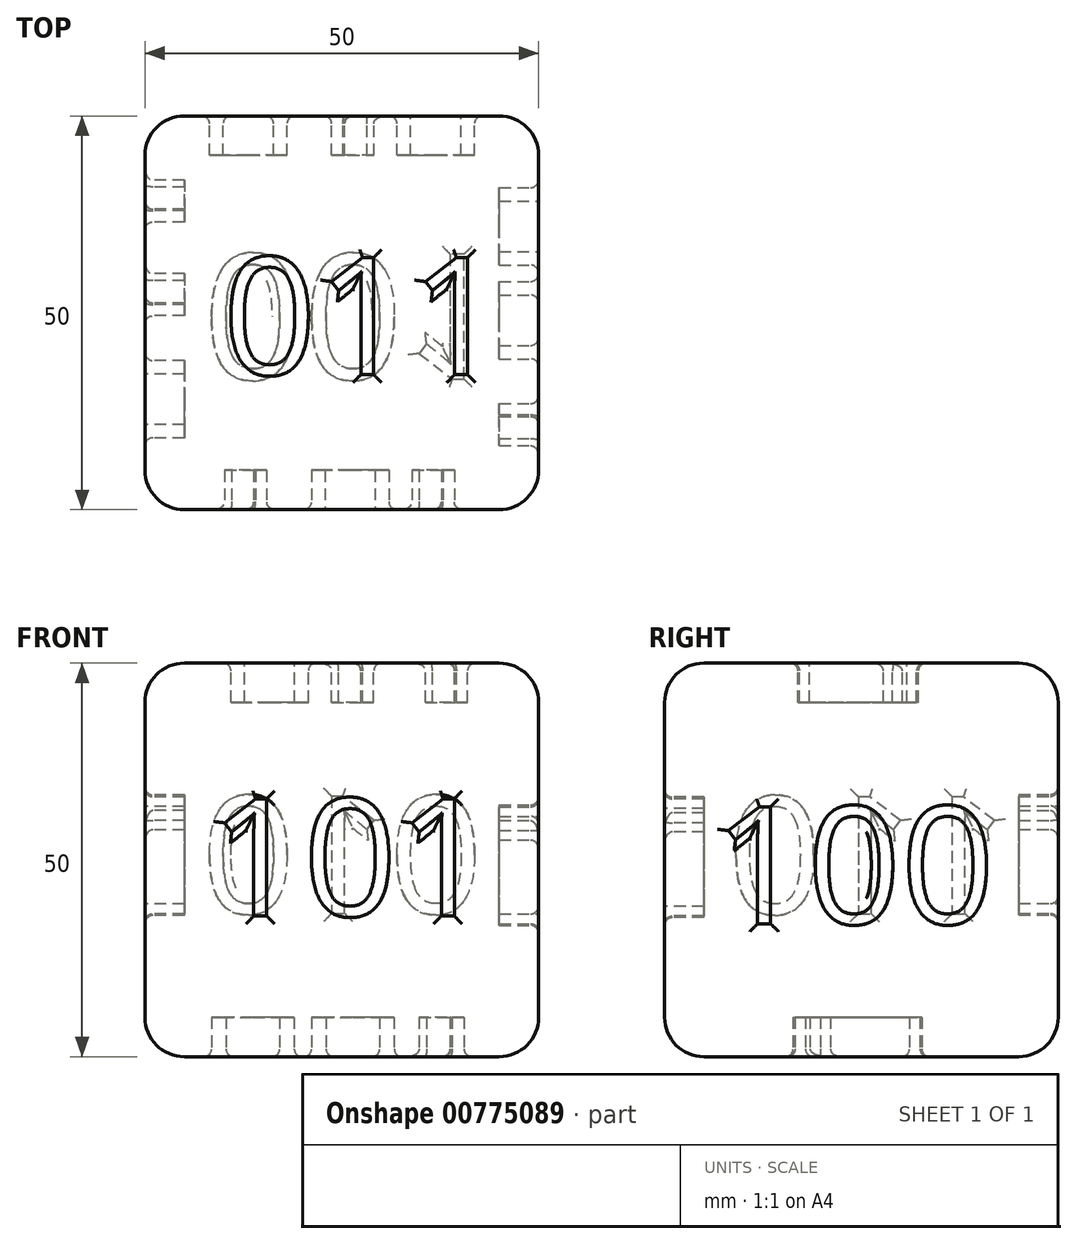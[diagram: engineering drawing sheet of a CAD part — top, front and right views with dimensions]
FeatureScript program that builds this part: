
annotation { "Feature Type Name" : "Feature", "Feature Type Description" : "" }
export const myFeature = defineFeature(function(context is Context, id is Id, definition is map)
    precondition{}
    {
        {
            var Q0;
            Q0=qCreatedBy(makeId("Top.planeOp"),FACE);
            var sketch = newSketch(context, id + "F0", { "sketchPlane" : qUnion([Q0])});
            skPoint(sketch, "E0.middle", {"position": v(0, 0) * mm});
            skLineSegment(sketch, "E1.bottom", {"start": v(25, -25) * mm, "end": v(-25, -25) * mm});
            skLineSegment(sketch, "E1.top", {"start": v(25, 25) * mm, "end": v(-25, 25) * mm});
            skLineSegment(sketch, "E1.left", {"start": v(25, -25) * mm, "end": v(25, 25) * mm});
            skLineSegment(sketch, "E1.right", {"start": v(-25, -25) * mm, "end": v(-25, 25) * mm});
            skSolve(sketch);
        }
        {
            var Q0;
            Q0 = qSketchRegion(id + "F0", true);
            extrude(context, id + "F1", {"entities" : qUnion([Q0]), "depth" : 50 * mm, "offsetDistance" : 25 * mm});
        }
        {
            var Q0;
            Q0=makeQuery(id+"F1.opExtrude","CAP_FACE",FACE,{"disambiguationData":[OSD([sQuery(id+"F0.wireOp",EDGE,"E1.bottom"),sQuery(id+"F0.wireOp",EDGE,"E1.top"),sQuery(id+"F0.wireOp",EDGE,"E1.left"),sQuery(id+"F0.wireOp",EDGE,"E1.right")])],"isStart":true});
            var Q1;
            Q1=makeQuery(id+"F1.opExtrude","SWEPT_FACE",FACE,{"disambiguationData":[OSD([sQuery(id+"F0.wireOp",EDGE,"E1.left")])]});
            var Q2;
            Q2=makeQuery(id+"F1.opExtrude","SWEPT_EDGE",EDGE,{"disambiguationData":[OSD([sQuery(id+"F0.wireOp",EDGE,"E1.bottom"),sQuery(id+"F0.wireOp",EDGE,"E1.right")])]});
            var Q3;
            Q3=makeQuery(id+"F1.opExtrude","CAP_FACE",FACE,{"disambiguationData":[OSD([sQuery(id+"F0.wireOp",EDGE,"E1.bottom"),sQuery(id+"F0.wireOp",EDGE,"E1.top"),sQuery(id+"F0.wireOp",EDGE,"E1.left"),sQuery(id+"F0.wireOp",EDGE,"E1.right")])],"isStart":false});
            var Q4;
            Q4=makeQuery(id+"F1.opExtrude","SWEPT_FACE",FACE,{"disambiguationData":[OSD([sQuery(id+"F0.wireOp",EDGE,"E1.right")])]});
            fillet(context, id + "F2", {"entities" : qUnion([Q0, Q1, Q2, Q3, Q4]), "radius" : 5 * mm, "tangentPropagation" : true, "allowEdgeOverflow" : false});
        }
        {
            var Q0;
            Q0=makeQuery(id+"F1.opExtrude","CAP_FACE",FACE,{"disambiguationData":[OSD([sQuery(id+"F0.wireOp",EDGE,"E1.bottom"),sQuery(id+"F0.wireOp",EDGE,"E1.top"),sQuery(id+"F0.wireOp",EDGE,"E1.left"),sQuery(id+"F0.wireOp",EDGE,"E1.right")])],"isStart":true});
            var sketch = newSketch(context, id + "F3", { "sketchPlane" : qUnion([Q0])});
            skText(sketch, "E2", { "text": "001\n", "fontName": "OpenSans-Regular.ttf"});
            const initialGuessF3  = {"E2": [-0.01764, -0.00745, 1, 0, 0.016]};
            skSetInitialGuess(sketch, initialGuessF3);
            skSolve(sketch);
        }
        {
            var Q0;
            Q0 = qSketchRegion(id + "F3", true);
            extrude(context, id + "F4", {"entities" : qUnion([Q0]), "operationType" : NewBodyOperationType.REMOVE, "oppositeDirection" : true, "depth" : 5 * mm, "offsetDistance" : 25 * mm});
        }
        {
            var Q0;
            Q0=makeQuery(id+"F4.boolean.opBoolean","COPY",EDGE,{"derivedFrom":makeQuery(id+"F4.opExtrude","CAP_EDGE",EDGE,{"disambiguationData":[OSD([sQuery(id+"F3.wireOp",EDGE,"E2.sketch_text.stroke-4")])],"isStart":true})});
            var Q1;
            Q1=makeQuery(id+"F4.boolean.opBoolean","COPY",EDGE,{"derivedFrom":makeQuery(id+"F4.opExtrude","CAP_EDGE",EDGE,{"disambiguationData":[OSD([sQuery(id+"F3.wireOp",EDGE,"E2.sketch_text.stroke-3")])],"isStart":true})});
            var Q2;
            Q2=makeQuery(id+"F4.boolean.opBoolean","COPY",EDGE,{"derivedFrom":makeQuery(id+"F4.opExtrude","CAP_EDGE",EDGE,{"disambiguationData":[OSD([sQuery(id+"F3.wireOp",EDGE,"E2.sketch_text.stroke-2")])],"isStart":true})});
            var Q3;
            Q3=makeQuery(id+"F4.boolean.opBoolean","COPY",EDGE,{"derivedFrom":makeQuery(id+"F4.opExtrude","CAP_EDGE",EDGE,{"disambiguationData":[OSD([sQuery(id+"F3.wireOp",EDGE,"E2.sketch_text.stroke-1")])],"isStart":true})});
            var Q4;
            {var subQ0=sQuery(id+"F0.wireOp",EDGE,"E1.right");var subQ1=sQuery(id+"F0.wireOp",EDGE,"E1.top");var subQ2=sQuery(id+"F0.wireOp",EDGE,"E1.bottom");var subQ3=sQuery(id+"F0.wireOp",EDGE,"E1.left");Q4=makeQuery(id+"F4.boolean.opBoolean","SPLIT",FACE,{"disambiguationData":[TD([makeQuery(id+"F4.opExtrude","SWEPT_FACE",FACE,{"disambiguationData":[OSD([sQuery(id+"F3.wireOp",EDGE,"E2.sketch_text.stroke-0")])]})])],"derivedFrom":makeQuery(id+"F1.opExtrude","CAP_FACE",FACE,{"disambiguationData":[OSD([subQ2,subQ1,subQ3,subQ0])],"isStart":true})});}
            var Q5;
            Q5=makeQuery(id+"F4.boolean.opBoolean","COPY",EDGE,{"derivedFrom":makeQuery(id+"F4.opExtrude","CAP_EDGE",EDGE,{"disambiguationData":[OSD([sQuery(id+"F3.wireOp",EDGE,"E2.sketch_text.stroke-11")])],"isStart":true})});
            var Q6;
            Q6=makeQuery(id+"F4.boolean.opBoolean","SPLIT",FACE,{"disambiguationData":[TD([makeQuery(id+"F4.opExtrude","SWEPT_FACE",FACE,{"disambiguationData":[OSD([sQuery(id+"F3.wireOp",EDGE,"E2.sketch_text.stroke-8")])]})])],"derivedFrom":makeQuery(id+"F1.opExtrude","CAP_FACE",FACE,{"disambiguationData":[OSD([sQuery(id+"F0.wireOp",EDGE,"E1.bottom"),sQuery(id+"F0.wireOp",EDGE,"E1.top"),sQuery(id+"F0.wireOp",EDGE,"E1.left"),sQuery(id+"F0.wireOp",EDGE,"E1.right")])],"isStart":true})});
            var Q7;
            Q7=makeQuery(id+"F4.boolean.opBoolean","SPLIT",FACE,{"disambiguationData":[TD([makeQuery(id+"F4.opExtrude","SWEPT_FACE",FACE,{"disambiguationData":[OSD([sQuery(id+"F3.wireOp",EDGE,"E2.sketch_text.stroke-24")])]})])],"derivedFrom":makeQuery(id+"F1.opExtrude","CAP_FACE",FACE,{"disambiguationData":[OSD([sQuery(id+"F0.wireOp",EDGE,"E1.bottom"),sQuery(id+"F0.wireOp",EDGE,"E1.top"),sQuery(id+"F0.wireOp",EDGE,"E1.left"),sQuery(id+"F0.wireOp",EDGE,"E1.right")])],"isStart":true})});
            var Q8;
            Q8=makeQuery(id+"F4.boolean.opBoolean","COPY",EDGE,{"derivedFrom":makeQuery(id+"F4.opExtrude","CAP_EDGE",EDGE,{"disambiguationData":[OSD([sQuery(id+"F3.wireOp",EDGE,"E2.sketch_text.stroke-33")])],"isStart":true})});
            fillet(context, id + "F5", {"entities" : qUnion([Q0, Q1, Q2, Q3, Q4, Q5, Q6, Q7, Q8]), "radius" : 1 * mm, "tangentPropagation" : true, "allowEdgeOverflow" : false});
        }
        {
            var Q0;
            Q0=makeQuery(id+"F1.opExtrude","SWEPT_FACE",FACE,{"disambiguationData":[OSD([sQuery(id+"F0.wireOp",EDGE,"E1.top")])]});
            var sketch = newSketch(context, id + "F6", { "sketchPlane" : qUnion([Q0])});
            skText(sketch, "E3", { "text": "010", "fontName": "OpenSans-Regular.ttf"});
            const initialGuessF6  = {"E3": [-0.0179, 0.0182, 1, 0, 0.015]};
            skSetInitialGuess(sketch, initialGuessF6);
            skSolve(sketch);
        }
        {
            var Q0;
            Q0 = qSketchRegion(id + "F6", true);
            extrude(context, id + "F7", {"entities" : qUnion([Q0]), "operationType" : NewBodyOperationType.REMOVE, "oppositeDirection" : true, "depth" : 5 * mm, "offsetDistance" : 25 * mm});
        }
        {
            var Q0;
            Q0=makeQuery(id+"F7.boolean.opBoolean","COPY",EDGE,{"derivedFrom":makeQuery(id+"F7.opExtrude","CAP_EDGE",EDGE,{"disambiguationData":[OSD([sQuery(id+"F6.wireOp",EDGE,"E3.sketch_text.stroke-2")])],"isStart":true})});
            var Q1;
            Q1=makeQuery(id+"F7.boolean.opBoolean","COPY",EDGE,{"derivedFrom":makeQuery(id+"F7.opExtrude","CAP_EDGE",EDGE,{"disambiguationData":[OSD([sQuery(id+"F6.wireOp",EDGE,"E3.sketch_text.stroke-3")])],"isStart":true})});
            var Q2;
            Q2=makeQuery(id+"F7.boolean.opBoolean","COPY",EDGE,{"derivedFrom":makeQuery(id+"F7.opExtrude","CAP_EDGE",EDGE,{"disambiguationData":[OSD([sQuery(id+"F6.wireOp",EDGE,"E3.sketch_text.stroke-4")])],"isStart":true})});
            var Q3;
            Q3=makeQuery(id+"F7.boolean.opBoolean","COPY",EDGE,{"derivedFrom":makeQuery(id+"F7.opExtrude","CAP_EDGE",EDGE,{"disambiguationData":[OSD([sQuery(id+"F6.wireOp",EDGE,"E3.sketch_text.stroke-5")])],"isStart":true})});
            var Q4;
            Q4=makeQuery(id+"F7.boolean.opBoolean","COPY",EDGE,{"derivedFrom":makeQuery(id+"F7.opExtrude","CAP_EDGE",EDGE,{"disambiguationData":[OSD([sQuery(id+"F6.wireOp",EDGE,"E3.sketch_text.stroke-6")])],"isStart":true})});
            var Q5;
            Q5=makeQuery(id+"F7.boolean.opBoolean","COPY",EDGE,{"derivedFrom":makeQuery(id+"F7.opExtrude","CAP_EDGE",EDGE,{"disambiguationData":[OSD([sQuery(id+"F6.wireOp",EDGE,"E3.sketch_text.stroke-7")])],"isStart":true})});
            var Q6;
            Q6=makeQuery(id+"F7.boolean.opBoolean","COPY",EDGE,{"derivedFrom":makeQuery(id+"F7.opExtrude","CAP_EDGE",EDGE,{"disambiguationData":[OSD([sQuery(id+"F6.wireOp",EDGE,"E3.sketch_text.stroke-0")])],"isStart":true})});
            var Q7;
            Q7=makeQuery(id+"F7.boolean.opBoolean","COPY",EDGE,{"derivedFrom":makeQuery(id+"F7.opExtrude","CAP_EDGE",EDGE,{"disambiguationData":[OSD([sQuery(id+"F6.wireOp",EDGE,"E3.sketch_text.stroke-1")])],"isStart":true})});
            var Q8;
            Q8=makeQuery(id+"F7.boolean.opBoolean","COPY",EDGE,{"derivedFrom":makeQuery(id+"F7.opExtrude","CAP_EDGE",EDGE,{"disambiguationData":[OSD([sQuery(id+"F6.wireOp",EDGE,"E3.sketch_text.stroke-11")])],"isStart":true})});
            var Q9;
            Q9=makeQuery(id+"F7.boolean.opBoolean","COPY",EDGE,{"derivedFrom":makeQuery(id+"F7.opExtrude","CAP_EDGE",EDGE,{"disambiguationData":[OSD([sQuery(id+"F6.wireOp",EDGE,"E3.sketch_text.stroke-12")])],"isStart":true})});
            var Q10;
            Q10=makeQuery(id+"F7.boolean.opBoolean","COPY",EDGE,{"derivedFrom":makeQuery(id+"F7.opExtrude","CAP_EDGE",EDGE,{"disambiguationData":[OSD([sQuery(id+"F6.wireOp",EDGE,"E3.sketch_text.stroke-13")])],"isStart":true})});
            var Q11;
            Q11=makeQuery(id+"F7.boolean.opBoolean","COPY",EDGE,{"derivedFrom":makeQuery(id+"F7.opExtrude","CAP_EDGE",EDGE,{"disambiguationData":[OSD([sQuery(id+"F6.wireOp",EDGE,"E3.sketch_text.stroke-10")])],"isStart":true})});
            var Q12;
            Q12=makeQuery(id+"F7.boolean.opBoolean","COPY",EDGE,{"derivedFrom":makeQuery(id+"F7.opExtrude","CAP_EDGE",EDGE,{"disambiguationData":[OSD([sQuery(id+"F6.wireOp",EDGE,"E3.sketch_text.stroke-9")])],"isStart":true})});
            var Q13;
            Q13=makeQuery(id+"F7.boolean.opBoolean","COPY",EDGE,{"derivedFrom":makeQuery(id+"F7.opExtrude","CAP_EDGE",EDGE,{"disambiguationData":[OSD([sQuery(id+"F6.wireOp",EDGE,"E3.sketch_text.stroke-8")])],"isStart":true})});
            var Q14;
            Q14=makeQuery(id+"F7.boolean.opBoolean","COPY",EDGE,{"derivedFrom":makeQuery(id+"F7.opExtrude","CAP_EDGE",EDGE,{"disambiguationData":[OSD([sQuery(id+"F6.wireOp",EDGE,"E3.sketch_text.stroke-15")])],"isStart":true})});
            var Q15;
            Q15=makeQuery(id+"F7.boolean.opBoolean","COPY",EDGE,{"derivedFrom":makeQuery(id+"F7.opExtrude","CAP_EDGE",EDGE,{"disambiguationData":[OSD([sQuery(id+"F6.wireOp",EDGE,"E3.sketch_text.stroke-14")])],"isStart":true})});
            var Q16;
            Q16=makeQuery(id+"F7.boolean.opBoolean","COPY",EDGE,{"derivedFrom":makeQuery(id+"F7.opExtrude","CAP_EDGE",EDGE,{"disambiguationData":[OSD([sQuery(id+"F6.wireOp",EDGE,"E3.sketch_text.stroke-17")])],"isStart":true})});
            var Q17;
            Q17=makeQuery(id+"F7.boolean.opBoolean","COPY",EDGE,{"derivedFrom":makeQuery(id+"F7.opExtrude","CAP_EDGE",EDGE,{"disambiguationData":[OSD([sQuery(id+"F6.wireOp",EDGE,"E3.sketch_text.stroke-18")])],"isStart":true})});
            var Q18;
            Q18=makeQuery(id+"F7.boolean.opBoolean","COPY",EDGE,{"derivedFrom":makeQuery(id+"F7.opExtrude","CAP_EDGE",EDGE,{"disambiguationData":[OSD([sQuery(id+"F6.wireOp",EDGE,"E3.sketch_text.stroke-23")])],"isStart":true})});
            var Q19;
            Q19=makeQuery(id+"F7.boolean.opBoolean","COPY",EDGE,{"derivedFrom":makeQuery(id+"F7.opExtrude","CAP_EDGE",EDGE,{"disambiguationData":[OSD([sQuery(id+"F6.wireOp",EDGE,"E3.sketch_text.stroke-24")])],"isStart":true})});
            var Q20;
            Q20=makeQuery(id+"F7.boolean.opBoolean","COPY",EDGE,{"derivedFrom":makeQuery(id+"F7.opExtrude","CAP_EDGE",EDGE,{"disambiguationData":[OSD([sQuery(id+"F6.wireOp",EDGE,"E3.sketch_text.stroke-22")])],"isStart":true})});
            var Q21;
            Q21=makeQuery(id+"F7.boolean.opBoolean","COPY",EDGE,{"derivedFrom":makeQuery(id+"F7.opExtrude","CAP_EDGE",EDGE,{"disambiguationData":[OSD([sQuery(id+"F6.wireOp",EDGE,"E3.sketch_text.stroke-21")])],"isStart":true})});
            var Q22;
            Q22=makeQuery(id+"F7.boolean.opBoolean","COPY",EDGE,{"derivedFrom":makeQuery(id+"F7.opExtrude","CAP_EDGE",EDGE,{"disambiguationData":[OSD([sQuery(id+"F6.wireOp",EDGE,"E3.sketch_text.stroke-20")])],"isStart":true})});
            var Q23;
            Q23=makeQuery(id+"F7.boolean.opBoolean","COPY",EDGE,{"derivedFrom":makeQuery(id+"F7.opExtrude","CAP_EDGE",EDGE,{"disambiguationData":[OSD([sQuery(id+"F6.wireOp",EDGE,"E3.sketch_text.stroke-16")])],"isStart":true})});
            var Q24;
            Q24=makeQuery(id+"F7.boolean.opBoolean","COPY",EDGE,{"derivedFrom":makeQuery(id+"F7.opExtrude","CAP_EDGE",EDGE,{"disambiguationData":[OSD([sQuery(id+"F6.wireOp",EDGE,"E3.sketch_text.stroke-33")])],"isStart":true})});
            var Q25;
            Q25=makeQuery(id+"F7.boolean.opBoolean","COPY",EDGE,{"derivedFrom":makeQuery(id+"F7.opExtrude","CAP_EDGE",EDGE,{"disambiguationData":[OSD([sQuery(id+"F6.wireOp",EDGE,"E3.sketch_text.stroke-40")])],"isStart":true})});
            var Q26;
            Q26=makeQuery(id+"F7.boolean.opBoolean","COPY",EDGE,{"derivedFrom":makeQuery(id+"F7.opExtrude","CAP_EDGE",EDGE,{"disambiguationData":[OSD([sQuery(id+"F6.wireOp",EDGE,"E3.sketch_text.stroke-27")])],"isStart":true})});
            var Q27;
            Q27=makeQuery(id+"F7.boolean.opBoolean","COPY",EDGE,{"derivedFrom":makeQuery(id+"F7.opExtrude","CAP_EDGE",EDGE,{"disambiguationData":[OSD([sQuery(id+"F6.wireOp",EDGE,"E3.sketch_text.stroke-26")])],"isStart":true})});
            fillet(context, id + "F8", {"entities" : qUnion([Q0, Q1, Q2, Q3, Q4, Q5, Q6, Q7, Q8, Q9, Q10, Q11, Q12, Q13, Q14, Q15, Q16, Q17, Q18, Q19, Q20, Q21, Q22, Q23, Q24, Q25, Q26, Q27]), "radius" : 1 * mm, "tangentPropagation" : true, "allowEdgeOverflow" : false});
        }
        {
            var Q0;
            Q0=makeQuery(id+"F1.opExtrude","CAP_FACE",FACE,{"disambiguationData":[OSD([sQuery(id+"F0.wireOp",EDGE,"E1.bottom"),sQuery(id+"F0.wireOp",EDGE,"E1.top"),sQuery(id+"F0.wireOp",EDGE,"E1.left"),sQuery(id+"F0.wireOp",EDGE,"E1.right")])],"isStart":false});
            var sketch = newSketch(context, id + "F9", { "sketchPlane" : qUnion([Q0])});
            skText(sketch, "E4", { "text": "011\n", "fontName": "OpenSans-Regular.ttf"});
            const initialGuessF9  = {"E4": [-0.01512, -0.00786, 1, 0, 0.015]};
            skSetInitialGuess(sketch, initialGuessF9);
            skSolve(sketch);
        }
        {
            var Q0;
            Q0 = qSketchRegion(id + "F9", true);
            extrude(context, id + "F10", {"entities" : qUnion([Q0]), "operationType" : NewBodyOperationType.REMOVE, "oppositeDirection" : true, "depth" : 5 * mm, "offsetDistance" : 25 * mm});
        }
        {
            var Q0;
            Q0=makeQuery(id+"F10.boolean.opBoolean","COPY",EDGE,{"derivedFrom":makeQuery(id+"F10.opExtrude","CAP_EDGE",EDGE,{"disambiguationData":[OSD([sQuery(id+"F9.wireOp",EDGE,"E4.sketch_text.stroke-1")])],"isStart":true})});
            var Q1;
            Q1=makeQuery(id+"F10.boolean.opBoolean","COPY",EDGE,{"derivedFrom":makeQuery(id+"F10.opExtrude","CAP_EDGE",EDGE,{"disambiguationData":[OSD([sQuery(id+"F9.wireOp",EDGE,"E4.sketch_text.stroke-2")])],"isStart":true})});
            var Q2;
            Q2=makeQuery(id+"F10.boolean.opBoolean","COPY",EDGE,{"derivedFrom":makeQuery(id+"F10.opExtrude","CAP_EDGE",EDGE,{"disambiguationData":[OSD([sQuery(id+"F9.wireOp",EDGE,"E4.sketch_text.stroke-3")])],"isStart":true})});
            var Q3;
            Q3=makeQuery(id+"F10.boolean.opBoolean","COPY",EDGE,{"derivedFrom":makeQuery(id+"F10.opExtrude","CAP_EDGE",EDGE,{"disambiguationData":[OSD([sQuery(id+"F9.wireOp",EDGE,"E4.sketch_text.stroke-4")])],"isStart":true})});
            var Q4;
            Q4=makeQuery(id+"F10.boolean.opBoolean","COPY",EDGE,{"derivedFrom":makeQuery(id+"F10.opExtrude","CAP_EDGE",EDGE,{"disambiguationData":[OSD([sQuery(id+"F9.wireOp",EDGE,"E4.sketch_text.stroke-15")])],"isStart":true})});
            var Q5;
            Q5=makeQuery(id+"F10.boolean.opBoolean","COPY",EDGE,{"derivedFrom":makeQuery(id+"F10.opExtrude","CAP_EDGE",EDGE,{"disambiguationData":[OSD([sQuery(id+"F9.wireOp",EDGE,"E4.sketch_text.stroke-8")])],"isStart":true})});
            var Q6;
            Q6=makeQuery(id+"F10.boolean.opBoolean","COPY",EDGE,{"derivedFrom":makeQuery(id+"F10.opExtrude","CAP_EDGE",EDGE,{"disambiguationData":[OSD([sQuery(id+"F9.wireOp",EDGE,"E4.sketch_text.stroke-9")])],"isStart":true})});
            var Q7;
            Q7=makeQuery(id+"F10.boolean.opBoolean","COPY",EDGE,{"derivedFrom":makeQuery(id+"F10.opExtrude","CAP_EDGE",EDGE,{"disambiguationData":[OSD([sQuery(id+"F9.wireOp",EDGE,"E4.sketch_text.stroke-10")])],"isStart":true})});
            var Q8;
            Q8=makeQuery(id+"F10.boolean.opBoolean","COPY",EDGE,{"derivedFrom":makeQuery(id+"F10.opExtrude","CAP_EDGE",EDGE,{"disambiguationData":[OSD([sQuery(id+"F9.wireOp",EDGE,"E4.sketch_text.stroke-11")])],"isStart":true})});
            var Q9;
            Q9=makeQuery(id+"F10.boolean.opBoolean","COPY",EDGE,{"derivedFrom":makeQuery(id+"F10.opExtrude","CAP_EDGE",EDGE,{"disambiguationData":[OSD([sQuery(id+"F9.wireOp",EDGE,"E4.sketch_text.stroke-12")])],"isStart":true})});
            var Q10;
            Q10=makeQuery(id+"F10.boolean.opBoolean","COPY",EDGE,{"derivedFrom":makeQuery(id+"F10.opExtrude","CAP_EDGE",EDGE,{"disambiguationData":[OSD([sQuery(id+"F9.wireOp",EDGE,"E4.sketch_text.stroke-13")])],"isStart":true})});
            var Q11;
            Q11=makeQuery(id+"F10.boolean.opBoolean","COPY",EDGE,{"derivedFrom":makeQuery(id+"F10.opExtrude","CAP_EDGE",EDGE,{"disambiguationData":[OSD([sQuery(id+"F9.wireOp",EDGE,"E4.sketch_text.stroke-14")])],"isStart":true})});
            var Q12;
            Q12=makeQuery(id+"F10.boolean.opBoolean","COPY",EDGE,{"derivedFrom":makeQuery(id+"F10.opExtrude","CAP_EDGE",EDGE,{"disambiguationData":[OSD([sQuery(id+"F9.wireOp",EDGE,"E4.sketch_text.stroke-17")])],"isStart":true})});
            var Q13;
            Q13=makeQuery(id+"F10.boolean.opBoolean","COPY",EDGE,{"derivedFrom":makeQuery(id+"F10.opExtrude","CAP_EDGE",EDGE,{"disambiguationData":[OSD([sQuery(id+"F9.wireOp",EDGE,"E4.sketch_text.stroke-26")])],"isStart":true})});
            var Q14;
            Q14=makeQuery(id+"F10.boolean.opBoolean","COPY",EDGE,{"derivedFrom":makeQuery(id+"F10.opExtrude","CAP_EDGE",EDGE,{"disambiguationData":[OSD([sQuery(id+"F9.wireOp",EDGE,"E4.sketch_text.stroke-33")])],"isStart":true})});
            var Q15;
            Q15=makeQuery(id+"F10.boolean.opBoolean","COPY",EDGE,{"derivedFrom":makeQuery(id+"F10.opExtrude","CAP_EDGE",EDGE,{"disambiguationData":[OSD([sQuery(id+"F9.wireOp",EDGE,"E4.sketch_text.stroke-16")])],"isStart":true})});
            var Q16;
            Q16=makeQuery(id+"F10.boolean.opBoolean","COPY",EDGE,{"derivedFrom":makeQuery(id+"F10.opExtrude","CAP_EDGE",EDGE,{"disambiguationData":[OSD([sQuery(id+"F9.wireOp",EDGE,"E4.sketch_text.stroke-25")])],"isStart":true})});
            var Q17;
            Q17=makeQuery(id+"F10.boolean.opBoolean","COPY",EDGE,{"derivedFrom":makeQuery(id+"F10.opExtrude","CAP_EDGE",EDGE,{"disambiguationData":[OSD([sQuery(id+"F9.wireOp",EDGE,"E4.sketch_text.stroke-22")])],"isStart":true})});
            var Q18;
            Q18=makeQuery(id+"F10.boolean.opBoolean","COPY",EDGE,{"derivedFrom":makeQuery(id+"F10.opExtrude","CAP_EDGE",EDGE,{"disambiguationData":[OSD([sQuery(id+"F9.wireOp",EDGE,"E4.sketch_text.stroke-21")])],"isStart":true})});
            var Q19;
            Q19=makeQuery(id+"F10.boolean.opBoolean","COPY",EDGE,{"derivedFrom":makeQuery(id+"F10.opExtrude","CAP_EDGE",EDGE,{"disambiguationData":[OSD([sQuery(id+"F9.wireOp",EDGE,"E4.sketch_text.stroke-20")])],"isStart":true})});
            var Q20;
            Q20=makeQuery(id+"F10.boolean.opBoolean","COPY",EDGE,{"derivedFrom":makeQuery(id+"F10.opExtrude","CAP_EDGE",EDGE,{"disambiguationData":[OSD([sQuery(id+"F9.wireOp",EDGE,"E4.sketch_text.stroke-31")])],"isStart":true})});
            var Q21;
            Q21=makeQuery(id+"F10.boolean.opBoolean","COPY",EDGE,{"derivedFrom":makeQuery(id+"F10.opExtrude","CAP_EDGE",EDGE,{"disambiguationData":[OSD([sQuery(id+"F9.wireOp",EDGE,"E4.sketch_text.stroke-32")])],"isStart":true})});
            var Q22;
            Q22=makeQuery(id+"F10.boolean.opBoolean","COPY",EDGE,{"derivedFrom":makeQuery(id+"F10.opExtrude","CAP_EDGE",EDGE,{"disambiguationData":[OSD([sQuery(id+"F9.wireOp",EDGE,"E4.sketch_text.stroke-23")])],"isStart":true})});
            var Q23;
            Q23=makeQuery(id+"F10.boolean.opBoolean","COPY",EDGE,{"derivedFrom":makeQuery(id+"F10.opExtrude","CAP_EDGE",EDGE,{"disambiguationData":[OSD([sQuery(id+"F9.wireOp",EDGE,"E4.sketch_text.stroke-24")])],"isStart":true})});
            var Q24;
            Q24=makeQuery(id+"F10.boolean.opBoolean","COPY",EDGE,{"derivedFrom":makeQuery(id+"F10.opExtrude","CAP_EDGE",EDGE,{"disambiguationData":[OSD([sQuery(id+"F9.wireOp",EDGE,"E4.sketch_text.stroke-18")])],"isStart":true})});
            var Q25;
            Q25=makeQuery(id+"F10.boolean.opBoolean","COPY",EDGE,{"derivedFrom":makeQuery(id+"F10.opExtrude","CAP_EDGE",EDGE,{"disambiguationData":[OSD([sQuery(id+"F9.wireOp",EDGE,"E4.sketch_text.stroke-27")])],"isStart":true})});
            var Q26;
            Q26=makeQuery(id+"F10.boolean.opBoolean","COPY",EDGE,{"derivedFrom":makeQuery(id+"F10.opExtrude","CAP_EDGE",EDGE,{"disambiguationData":[OSD([sQuery(id+"F9.wireOp",EDGE,"E4.sketch_text.stroke-30")])],"isStart":true})});
            var Q27;
            Q27=makeQuery(id+"F10.boolean.opBoolean","COPY",EDGE,{"derivedFrom":makeQuery(id+"F10.opExtrude","CAP_EDGE",EDGE,{"disambiguationData":[OSD([sQuery(id+"F9.wireOp",EDGE,"E4.sketch_text.stroke-29")])],"isStart":true})});
            fillet(context, id + "F11", {"entities" : qUnion([Q0, Q1, Q2, Q3, Q4, Q5, Q6, Q7, Q8, Q9, Q10, Q11, Q12, Q13, Q14, Q15, Q16, Q17, Q18, Q19, Q20, Q21, Q22, Q23, Q24, Q25, Q26, Q27]), "radius" : 1 * mm, "tangentPropagation" : true, "allowEdgeOverflow" : false});
        }
        {
            var Q0;
            Q0=makeQuery(id+"F1.opExtrude","SWEPT_FACE",FACE,{"disambiguationData":[OSD([sQuery(id+"F0.wireOp",EDGE,"E1.left")])]});
            var sketch = newSketch(context, id + "F12", { "sketchPlane" : qUnion([Q0])});
            skText(sketch, "E5", { "text": "100", "fontName": "OpenSans-Regular.ttf"});
            const initialGuessF12  = {"E5": [-0.0188, 0.01688, 1, 0, 0.015]};
            skSetInitialGuess(sketch, initialGuessF12);
            skSolve(sketch);
        }
        {
            var Q0;
            Q0=makeQuery(id+"F12.imprint","IMPRINT",FACE,{"disambiguationData":[TD([[makeQuery(id+"F12.imprint","IMPRINT",EDGE,{"derivedFrom":sQuery(id+"F12.wireOp",EDGE,"E5.sketch_text.stroke-0")}),-1.0]])]});
            var Q1;
            Q1=makeQuery(id+"F12.imprint","IMPRINT",FACE,{"disambiguationData":[TD([[makeQuery(id+"F12.imprint","IMPRINT",EDGE,{"derivedFrom":sQuery(id+"F12.wireOp",EDGE,"E5.sketch_text.stroke-9")}),-1.0]])]});
            var Q2;
            Q2=makeQuery(id+"F12.imprint","IMPRINT",FACE,{"disambiguationData":[TD([[makeQuery(id+"F12.imprint","IMPRINT",EDGE,{"derivedFrom":sQuery(id+"F12.wireOp",EDGE,"E5.sketch_text.stroke-25")}),-1.0]])]});
            extrude(context, id + "F13", {"entities" : qUnion([Q0, Q1, Q2]), "operationType" : NewBodyOperationType.REMOVE, "oppositeDirection" : true, "depth" : 5 * mm, "offsetDistance" : 25 * mm});
        }
        {
            var Q0;
            Q0=makeQuery(id+"F13.boolean.opBoolean","COPY",EDGE,{"derivedFrom":makeQuery(id+"F13.opExtrude","CAP_EDGE",EDGE,{"disambiguationData":[OSD([sQuery(id+"F12.wireOp",EDGE,"E5.sketch_text.stroke-8")])],"isStart":true})});
            var Q1;
            Q1=makeQuery(id+"F13.boolean.opBoolean","COPY",EDGE,{"derivedFrom":makeQuery(id+"F13.opExtrude","CAP_EDGE",EDGE,{"disambiguationData":[OSD([sQuery(id+"F12.wireOp",EDGE,"E5.sketch_text.stroke-6")])],"isStart":true})});
            var Q2;
            Q2=makeQuery(id+"F13.boolean.opBoolean","COPY",EDGE,{"derivedFrom":makeQuery(id+"F13.opExtrude","CAP_EDGE",EDGE,{"disambiguationData":[OSD([sQuery(id+"F12.wireOp",EDGE,"E5.sketch_text.stroke-7")])],"isStart":true})});
            var Q3;
            Q3=makeQuery(id+"F13.boolean.opBoolean","COPY",EDGE,{"derivedFrom":makeQuery(id+"F13.opExtrude","CAP_EDGE",EDGE,{"disambiguationData":[OSD([sQuery(id+"F12.wireOp",EDGE,"E5.sketch_text.stroke-5")])],"isStart":true})});
            var Q4;
            Q4=makeQuery(id+"F13.boolean.opBoolean","COPY",EDGE,{"derivedFrom":makeQuery(id+"F13.opExtrude","CAP_EDGE",EDGE,{"disambiguationData":[OSD([sQuery(id+"F12.wireOp",EDGE,"E5.sketch_text.stroke-4")])],"isStart":true})});
            var Q5;
            Q5=makeQuery(id+"F13.boolean.opBoolean","COPY",EDGE,{"derivedFrom":makeQuery(id+"F13.opExtrude","CAP_EDGE",EDGE,{"disambiguationData":[OSD([sQuery(id+"F12.wireOp",EDGE,"E5.sketch_text.stroke-1")])],"isStart":true})});
            var Q6;
            Q6=makeQuery(id+"F13.boolean.opBoolean","COPY",EDGE,{"derivedFrom":makeQuery(id+"F13.opExtrude","CAP_EDGE",EDGE,{"disambiguationData":[OSD([sQuery(id+"F12.wireOp",EDGE,"E5.sketch_text.stroke-0")])],"isStart":true})});
            var Q7;
            Q7=makeQuery(id+"F13.boolean.opBoolean","COPY",EDGE,{"derivedFrom":makeQuery(id+"F13.opExtrude","CAP_EDGE",EDGE,{"disambiguationData":[OSD([sQuery(id+"F12.wireOp",EDGE,"E5.sketch_text.stroke-3")])],"isStart":true})});
            var Q8;
            Q8=makeQuery(id+"F13.boolean.opBoolean","COPY",EDGE,{"derivedFrom":makeQuery(id+"F13.opExtrude","CAP_EDGE",EDGE,{"disambiguationData":[OSD([sQuery(id+"F12.wireOp",EDGE,"E5.sketch_text.stroke-12")])],"isStart":true})});
            var Q9;
            Q9=makeQuery(id+"F13.boolean.opBoolean","COPY",EDGE,{"derivedFrom":makeQuery(id+"F13.opExtrude","CAP_EDGE",EDGE,{"disambiguationData":[OSD([sQuery(id+"F12.wireOp",EDGE,"E5.sketch_text.stroke-20")])],"isStart":true})});
            var Q10;
            Q10=makeQuery(id+"F13.boolean.opBoolean","COPY",EDGE,{"derivedFrom":makeQuery(id+"F13.opExtrude","CAP_EDGE",EDGE,{"disambiguationData":[OSD([sQuery(id+"F12.wireOp",EDGE,"E5.sketch_text.stroke-34")])],"isStart":true})});
            var Q11;
            Q11=makeQuery(id+"F13.boolean.opBoolean","COPY",EDGE,{"derivedFrom":makeQuery(id+"F13.opExtrude","CAP_EDGE",EDGE,{"disambiguationData":[OSD([sQuery(id+"F12.wireOp",EDGE,"E5.sketch_text.stroke-28")])],"isStart":true})});
            var Q12;
            Q12=makeQuery(id+"F13.boolean.opBoolean","COPY",EDGE,{"derivedFrom":makeQuery(id+"F13.opExtrude","CAP_EDGE",EDGE,{"disambiguationData":[OSD([sQuery(id+"F12.wireOp",EDGE,"E5.sketch_text.stroke-2")])],"isStart":true})});
            fillet(context, id + "F14", {"entities" : qUnion([Q0, Q1, Q2, Q3, Q4, Q5, Q6, Q7, Q8, Q9, Q10, Q11, Q12]), "radius" : 1 * mm, "tangentPropagation" : true, "allowEdgeOverflow" : false});
        }
        {
            var Q0;
            Q0=makeQuery(id+"F1.opExtrude","SWEPT_FACE",FACE,{"disambiguationData":[OSD([sQuery(id+"F0.wireOp",EDGE,"E1.bottom")])]});
            var sketch = newSketch(context, id + "F15", { "sketchPlane" : qUnion([Q0])});
            skText(sketch, "E6", { "text": "101\n", "fontName": "OpenSans-Regular.ttf"});
            const initialGuessF15  = {"E6": [-0.0168, 0.01787, 1, 0, 0.015]};
            skSetInitialGuess(sketch, initialGuessF15);
            skSolve(sketch);
        }
        {
            var Q0;
            Q0=makeQuery(id+"F15.imprint","IMPRINT",FACE,{"disambiguationData":[TD([[makeQuery(id+"F15.imprint","IMPRINT",EDGE,{"derivedFrom":sQuery(id+"F15.wireOp",EDGE,"E6.sketch_text.stroke-0")}),-1.0]])]});
            var Q1;
            Q1=makeQuery(id+"F15.imprint","IMPRINT",FACE,{"disambiguationData":[TD([[makeQuery(id+"F15.imprint","IMPRINT",EDGE,{"derivedFrom":sQuery(id+"F15.wireOp",EDGE,"E6.sketch_text.stroke-9")}),-1.0]])]});
            var Q2;
            Q2=makeQuery(id+"F15.imprint","IMPRINT",FACE,{"disambiguationData":[TD([[makeQuery(id+"F15.imprint","IMPRINT",EDGE,{"derivedFrom":sQuery(id+"F15.wireOp",EDGE,"E6.sketch_text.stroke-25")}),-1.0]])]});
            extrude(context, id + "F16", {"entities" : qUnion([Q0, Q1, Q2]), "operationType" : NewBodyOperationType.REMOVE, "oppositeDirection" : true, "depth" : 5 * mm, "offsetDistance" : 25 * mm});
        }
        {
            var Q0;
            Q0=makeQuery(id+"F16.boolean.opBoolean","COPY",EDGE,{"derivedFrom":makeQuery(id+"F16.opExtrude","CAP_EDGE",EDGE,{"disambiguationData":[OSD([sQuery(id+"F15.wireOp",EDGE,"E6.sketch_text.stroke-1")])],"isStart":true})});
            var Q1;
            Q1=makeQuery(id+"F16.boolean.opBoolean","COPY",EDGE,{"derivedFrom":makeQuery(id+"F16.opExtrude","CAP_EDGE",EDGE,{"disambiguationData":[OSD([sQuery(id+"F15.wireOp",EDGE,"E6.sketch_text.stroke-2")])],"isStart":true})});
            var Q2;
            Q2=makeQuery(id+"F16.boolean.opBoolean","COPY",EDGE,{"derivedFrom":makeQuery(id+"F16.opExtrude","CAP_EDGE",EDGE,{"disambiguationData":[OSD([sQuery(id+"F15.wireOp",EDGE,"E6.sketch_text.stroke-6")])],"isStart":true})});
            var Q3;
            Q3=makeQuery(id+"F16.boolean.opBoolean","COPY",EDGE,{"derivedFrom":makeQuery(id+"F16.opExtrude","CAP_EDGE",EDGE,{"disambiguationData":[OSD([sQuery(id+"F15.wireOp",EDGE,"E6.sketch_text.stroke-4")])],"isStart":true})});
            var Q4;
            Q4=makeQuery(id+"F16.boolean.opBoolean","COPY",EDGE,{"derivedFrom":makeQuery(id+"F16.opExtrude","CAP_EDGE",EDGE,{"disambiguationData":[OSD([sQuery(id+"F15.wireOp",EDGE,"E6.sketch_text.stroke-5")])],"isStart":true})});
            var Q5;
            Q5=makeQuery(id+"F16.boolean.opBoolean","COPY",EDGE,{"derivedFrom":makeQuery(id+"F16.opExtrude","CAP_EDGE",EDGE,{"disambiguationData":[OSD([sQuery(id+"F15.wireOp",EDGE,"E6.sketch_text.stroke-7")])],"isStart":true})});
            var Q6;
            Q6=makeQuery(id+"F16.boolean.opBoolean","COPY",EDGE,{"derivedFrom":makeQuery(id+"F16.opExtrude","CAP_EDGE",EDGE,{"disambiguationData":[OSD([sQuery(id+"F15.wireOp",EDGE,"E6.sketch_text.stroke-8")])],"isStart":true})});
            var Q7;
            Q7=makeQuery(id+"F16.boolean.opBoolean","COPY",EDGE,{"derivedFrom":makeQuery(id+"F16.opExtrude","CAP_EDGE",EDGE,{"disambiguationData":[OSD([sQuery(id+"F15.wireOp",EDGE,"E6.sketch_text.stroke-3")])],"isStart":true})});
            var Q8;
            Q8=makeQuery(id+"F16.boolean.opBoolean","COPY",EDGE,{"derivedFrom":makeQuery(id+"F16.opExtrude","CAP_EDGE",EDGE,{"disambiguationData":[OSD([sQuery(id+"F15.wireOp",EDGE,"E6.sketch_text.stroke-0")])],"isStart":true})});
            var Q9;
            Q9=makeQuery(id+"F16.boolean.opBoolean","COPY",EDGE,{"derivedFrom":makeQuery(id+"F16.opExtrude","CAP_EDGE",EDGE,{"disambiguationData":[OSD([sQuery(id+"F15.wireOp",EDGE,"E6.sketch_text.stroke-17")])],"isStart":true})});
            var Q10;
            Q10=makeQuery(id+"F16.boolean.opBoolean","COPY",EDGE,{"derivedFrom":makeQuery(id+"F16.opExtrude","CAP_EDGE",EDGE,{"disambiguationData":[OSD([sQuery(id+"F15.wireOp",EDGE,"E6.sketch_text.stroke-15")])],"isStart":true})});
            var Q11;
            Q11=makeQuery(id+"F16.boolean.opBoolean","COPY",EDGE,{"derivedFrom":makeQuery(id+"F16.opExtrude","CAP_EDGE",EDGE,{"disambiguationData":[OSD([sQuery(id+"F15.wireOp",EDGE,"E6.sketch_text.stroke-30")])],"isStart":true})});
            var Q12;
            Q12=makeQuery(id+"F16.boolean.opBoolean","COPY",EDGE,{"derivedFrom":makeQuery(id+"F16.opExtrude","CAP_EDGE",EDGE,{"disambiguationData":[OSD([sQuery(id+"F15.wireOp",EDGE,"E6.sketch_text.stroke-26")])],"isStart":true})});
            var Q13;
            Q13=makeQuery(id+"F16.boolean.opBoolean","COPY",EDGE,{"derivedFrom":makeQuery(id+"F16.opExtrude","CAP_EDGE",EDGE,{"disambiguationData":[OSD([sQuery(id+"F15.wireOp",EDGE,"E6.sketch_text.stroke-32")])],"isStart":true})});
            var Q14;
            Q14=makeQuery(id+"F16.boolean.opBoolean","COPY",EDGE,{"derivedFrom":makeQuery(id+"F16.opExtrude","CAP_EDGE",EDGE,{"disambiguationData":[OSD([sQuery(id+"F15.wireOp",EDGE,"E6.sketch_text.stroke-31")])],"isStart":true})});
            var Q15;
            Q15=makeQuery(id+"F16.boolean.opBoolean","COPY",EDGE,{"derivedFrom":makeQuery(id+"F16.opExtrude","CAP_EDGE",EDGE,{"disambiguationData":[OSD([sQuery(id+"F15.wireOp",EDGE,"E6.sketch_text.stroke-29")])],"isStart":true})});
            var Q16;
            Q16=makeQuery(id+"F16.boolean.opBoolean","COPY",EDGE,{"derivedFrom":makeQuery(id+"F16.opExtrude","CAP_EDGE",EDGE,{"disambiguationData":[OSD([sQuery(id+"F15.wireOp",EDGE,"E6.sketch_text.stroke-28")])],"isStart":true})});
            var Q17;
            Q17=makeQuery(id+"F16.boolean.opBoolean","COPY",EDGE,{"derivedFrom":makeQuery(id+"F16.opExtrude","CAP_EDGE",EDGE,{"disambiguationData":[OSD([sQuery(id+"F15.wireOp",EDGE,"E6.sketch_text.stroke-27")])],"isStart":true})});
            var Q18;
            Q18=makeQuery(id+"F16.boolean.opBoolean","COPY",EDGE,{"derivedFrom":makeQuery(id+"F16.opExtrude","CAP_EDGE",EDGE,{"disambiguationData":[OSD([sQuery(id+"F15.wireOp",EDGE,"E6.sketch_text.stroke-33")])],"isStart":true})});
            var Q19;
            Q19=makeQuery(id+"F16.boolean.opBoolean","COPY",EDGE,{"derivedFrom":makeQuery(id+"F16.opExtrude","CAP_EDGE",EDGE,{"disambiguationData":[OSD([sQuery(id+"F15.wireOp",EDGE,"E6.sketch_text.stroke-25")])],"isStart":true})});
            fillet(context, id + "F17", {"entities" : qUnion([Q0, Q1, Q2, Q3, Q4, Q5, Q6, Q7, Q8, Q9, Q10, Q11, Q12, Q13, Q14, Q15, Q16, Q17, Q18, Q19]), "radius" : 1 * mm, "tangentPropagation" : true, "allowEdgeOverflow" : false});
        }
        {
            var Q0;
            Q0=makeQuery(id+"F1.opExtrude","SWEPT_FACE",FACE,{"disambiguationData":[OSD([sQuery(id+"F0.wireOp",EDGE,"E1.right")])]});
            var sketch = newSketch(context, id + "F18", { "sketchPlane" : qUnion([Q0])});
            skText(sketch, "E7", { "text": "110\n", "fontName": "OpenSans-Regular.ttf"});
            const initialGuessF18  = {"E7": [-0.0188, 0.01815, 1, 0, 0.015]};
            skSetInitialGuess(sketch, initialGuessF18);
            skSolve(sketch);
        }
        {
            var Q0;
            Q0 = qSketchRegion(id + "F18", true);
            extrude(context, id + "F19", {"entities" : qUnion([Q0]), "operationType" : NewBodyOperationType.REMOVE, "oppositeDirection" : true, "depth" : 5 * mm, "offsetDistance" : 25 * mm});
        }
        {
            var Q0;
            Q0=makeQuery(id+"F19.boolean.opBoolean","COPY",EDGE,{"derivedFrom":makeQuery(id+"F19.opExtrude","CAP_EDGE",EDGE,{"disambiguationData":[OSD([sQuery(id+"F18.wireOp",EDGE,"E7.sketch_text.stroke-1")])],"isStart":true})});
            var Q1;
            Q1=makeQuery(id+"F19.boolean.opBoolean","COPY",EDGE,{"derivedFrom":makeQuery(id+"F19.opExtrude","CAP_EDGE",EDGE,{"disambiguationData":[OSD([sQuery(id+"F18.wireOp",EDGE,"E7.sketch_text.stroke-2")])],"isStart":true})});
            var Q2;
            Q2=makeQuery(id+"F19.boolean.opBoolean","COPY",EDGE,{"derivedFrom":makeQuery(id+"F19.opExtrude","CAP_EDGE",EDGE,{"disambiguationData":[OSD([sQuery(id+"F18.wireOp",EDGE,"E7.sketch_text.stroke-7")])],"isStart":true})});
            var Q3;
            Q3=makeQuery(id+"F19.boolean.opBoolean","COPY",EDGE,{"derivedFrom":makeQuery(id+"F19.opExtrude","CAP_EDGE",EDGE,{"disambiguationData":[OSD([sQuery(id+"F18.wireOp",EDGE,"E7.sketch_text.stroke-8")])],"isStart":true})});
            var Q4;
            Q4=makeQuery(id+"F19.boolean.opBoolean","COPY",EDGE,{"derivedFrom":makeQuery(id+"F19.opExtrude","CAP_EDGE",EDGE,{"disambiguationData":[OSD([sQuery(id+"F18.wireOp",EDGE,"E7.sketch_text.stroke-6")])],"isStart":true})});
            var Q5;
            Q5=makeQuery(id+"F19.boolean.opBoolean","COPY",EDGE,{"derivedFrom":makeQuery(id+"F19.opExtrude","CAP_EDGE",EDGE,{"disambiguationData":[OSD([sQuery(id+"F18.wireOp",EDGE,"E7.sketch_text.stroke-4")])],"isStart":true})});
            var Q6;
            Q6=makeQuery(id+"F19.boolean.opBoolean","COPY",EDGE,{"derivedFrom":makeQuery(id+"F19.opExtrude","CAP_EDGE",EDGE,{"disambiguationData":[OSD([sQuery(id+"F18.wireOp",EDGE,"E7.sketch_text.stroke-5")])],"isStart":true})});
            var Q7;
            Q7=makeQuery(id+"F19.boolean.opBoolean","COPY",EDGE,{"derivedFrom":makeQuery(id+"F19.opExtrude","CAP_EDGE",EDGE,{"disambiguationData":[OSD([sQuery(id+"F18.wireOp",EDGE,"E7.sketch_text.stroke-3")])],"isStart":true})});
            var Q8;
            Q8=makeQuery(id+"F19.boolean.opBoolean","COPY",EDGE,{"derivedFrom":makeQuery(id+"F19.opExtrude","CAP_EDGE",EDGE,{"disambiguationData":[OSD([sQuery(id+"F18.wireOp",EDGE,"E7.sketch_text.stroke-0")])],"isStart":true})});
            var Q9;
            Q9=makeQuery(id+"F19.boolean.opBoolean","COPY",EDGE,{"derivedFrom":makeQuery(id+"F19.opExtrude","CAP_EDGE",EDGE,{"disambiguationData":[OSD([sQuery(id+"F18.wireOp",EDGE,"E7.sketch_text.stroke-16")])],"isStart":true})});
            var Q10;
            Q10=makeQuery(id+"F19.boolean.opBoolean","COPY",EDGE,{"derivedFrom":makeQuery(id+"F19.opExtrude","CAP_EDGE",EDGE,{"disambiguationData":[OSD([sQuery(id+"F18.wireOp",EDGE,"E7.sketch_text.stroke-17")])],"isStart":true})});
            var Q11;
            Q11=makeQuery(id+"F19.boolean.opBoolean","COPY",EDGE,{"derivedFrom":makeQuery(id+"F19.opExtrude","CAP_EDGE",EDGE,{"disambiguationData":[OSD([sQuery(id+"F18.wireOp",EDGE,"E7.sketch_text.stroke-15")])],"isStart":true})});
            var Q12;
            Q12=makeQuery(id+"F19.boolean.opBoolean","COPY",EDGE,{"derivedFrom":makeQuery(id+"F19.opExtrude","CAP_EDGE",EDGE,{"disambiguationData":[OSD([sQuery(id+"F18.wireOp",EDGE,"E7.sketch_text.stroke-14")])],"isStart":true})});
            var Q13;
            Q13=makeQuery(id+"F19.boolean.opBoolean","COPY",EDGE,{"derivedFrom":makeQuery(id+"F19.opExtrude","CAP_EDGE",EDGE,{"disambiguationData":[OSD([sQuery(id+"F18.wireOp",EDGE,"E7.sketch_text.stroke-13")])],"isStart":true})});
            var Q14;
            Q14=makeQuery(id+"F19.boolean.opBoolean","COPY",EDGE,{"derivedFrom":makeQuery(id+"F19.opExtrude","CAP_EDGE",EDGE,{"disambiguationData":[OSD([sQuery(id+"F18.wireOp",EDGE,"E7.sketch_text.stroke-12")])],"isStart":true})});
            var Q15;
            Q15=makeQuery(id+"F19.boolean.opBoolean","COPY",EDGE,{"derivedFrom":makeQuery(id+"F19.opExtrude","CAP_EDGE",EDGE,{"disambiguationData":[OSD([sQuery(id+"F18.wireOp",EDGE,"E7.sketch_text.stroke-10")])],"isStart":true})});
            var Q16;
            Q16=makeQuery(id+"F19.boolean.opBoolean","COPY",EDGE,{"derivedFrom":makeQuery(id+"F19.opExtrude","CAP_EDGE",EDGE,{"disambiguationData":[OSD([sQuery(id+"F18.wireOp",EDGE,"E7.sketch_text.stroke-11")])],"isStart":true})});
            var Q17;
            Q17=makeQuery(id+"F19.boolean.opBoolean","COPY",EDGE,{"derivedFrom":makeQuery(id+"F19.opExtrude","CAP_EDGE",EDGE,{"disambiguationData":[OSD([sQuery(id+"F18.wireOp",EDGE,"E7.sketch_text.stroke-33")])],"isStart":true})});
            var Q18;
            Q18=makeQuery(id+"F19.boolean.opBoolean","COPY",EDGE,{"derivedFrom":makeQuery(id+"F19.opExtrude","CAP_EDGE",EDGE,{"disambiguationData":[OSD([sQuery(id+"F18.wireOp",EDGE,"E7.sketch_text.stroke-24")])],"isStart":true})});
            var Q19;
            Q19=makeQuery(id+"F19.boolean.opBoolean","COPY",EDGE,{"derivedFrom":makeQuery(id+"F19.opExtrude","CAP_EDGE",EDGE,{"disambiguationData":[OSD([sQuery(id+"F18.wireOp",EDGE,"E7.sketch_text.stroke-9")])],"isStart":true})});
            fillet(context, id + "F20", {"entities" : qUnion([Q0, Q1, Q2, Q3, Q4, Q5, Q6, Q7, Q8, Q9, Q10, Q11, Q12, Q13, Q14, Q15, Q16, Q17, Q18, Q19]), "radius" : 1 * mm, "tangentPropagation" : true, "allowEdgeOverflow" : false});
        }
    });
